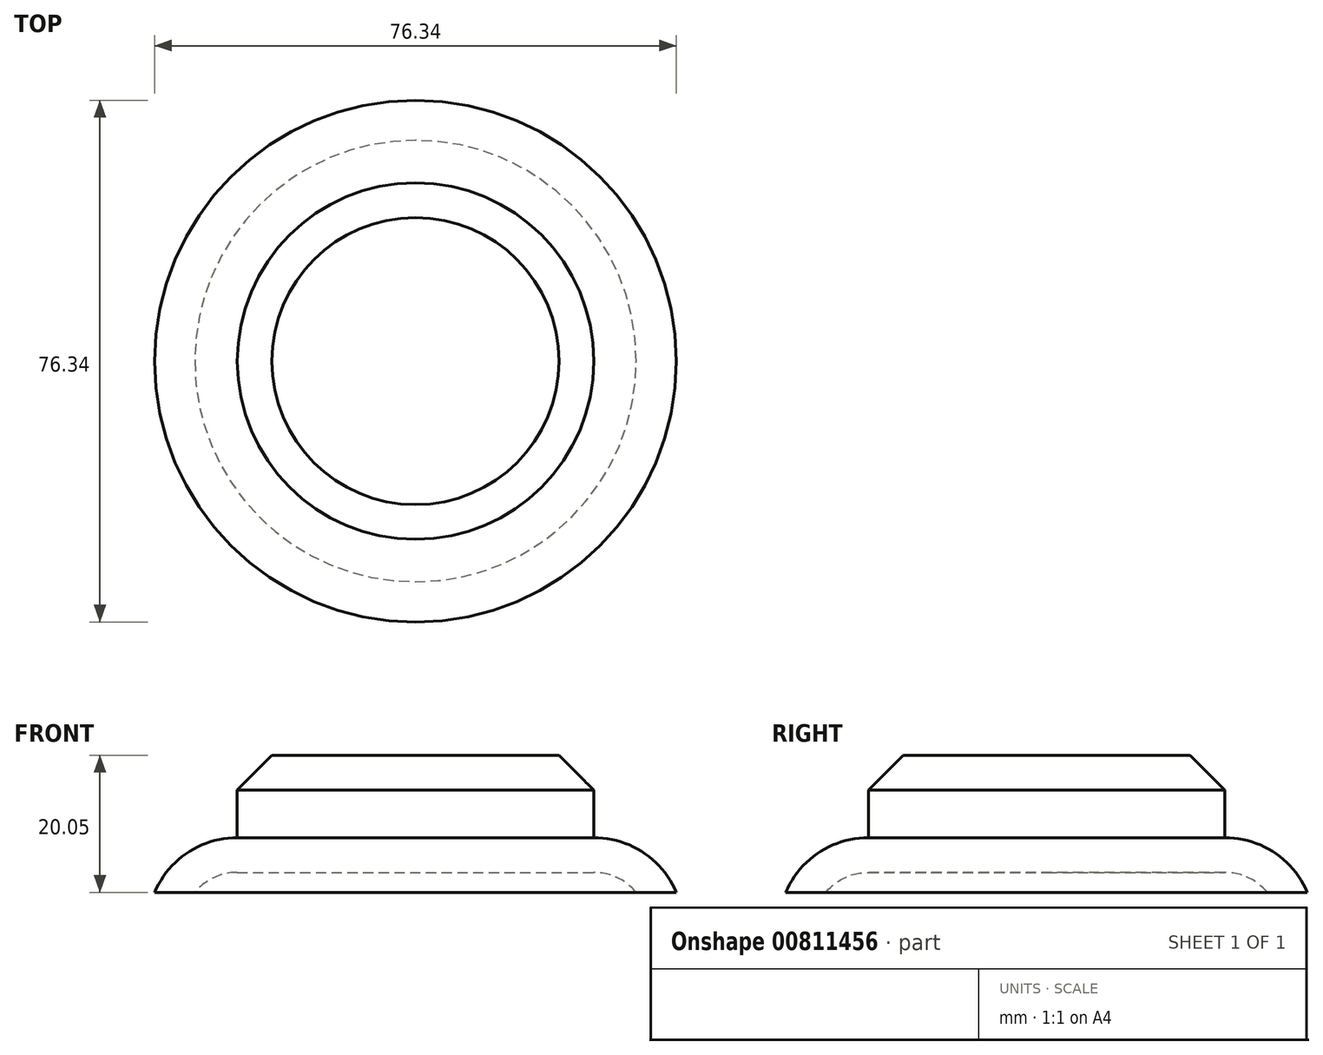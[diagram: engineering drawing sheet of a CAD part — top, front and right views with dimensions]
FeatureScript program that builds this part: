
annotation { "Feature Type Name" : "Feature", "Feature Type Description" : "" }
export const myFeature = defineFeature(function(context is Context, id is Id, definition is map)
    precondition{}
    {
        {
            var Q0;
            Q0=qCreatedBy(makeId("Top.planeOp"),FACE);
            var sketch = newSketch(context, id + "F0", { "sketchPlane" : qUnion([Q0])});
            skCircle(sketch, "E0", {"center": v(0, 0) * mm, "radius": 38.17 * mm});
            skSolve(sketch);
        }
        {
            var Q0;
            Q0=makeQuery(id+"F0.imprint","IMPRINT",FACE,{"disambiguationData":[TD([[makeQuery(id+"F0.imprint","IMPRINT",EDGE,{"derivedFrom":sQuery(id+"F0.wireOp",EDGE,"E0")}),1.0]])]});
            extrude(context, id + "F1", {"entities" : qUnion([Q0]), "depth" : 8 * mm, "offsetDistance" : 25.4 * mm});
        }
        {
            var Q0;
            Q0=makeQuery(id+"F1.opExtrude","CAP_FACE",FACE,{"disambiguationData":[OSD([sQuery(id+"F0.wireOp",EDGE,"E0")])],"isStart":false});
            fillet(context, id + "F2", {"entities" : qUnion([Q0]), "radius" : 13.13 * mm, "tangentPropagation" : true, "allowEdgeOverflow" : false});
        }
        {
            var Q0;
            Q0=makeQuery(id+"F1.opExtrude","CAP_FACE",FACE,{"disambiguationData":[OSD([sQuery(id+"F0.wireOp",EDGE,"E0")])],"isStart":true});
            shell(context, id + "F3", {"entities" : qUnion([Q0]), "thickness" : 5.08 * mm});
        }
        {
            var Q0;
            Q0=makeQuery(id+"F1.opExtrude","CAP_FACE",FACE,{"disambiguationData":[OSD([sQuery(id+"F0.wireOp",EDGE,"E0")])],"isStart":false});
            extrude(context, id + "F4", {"entities" : qUnion([Q0]), "operationType" : NewBodyOperationType.ADD, "depth" : 12.04 * mm, "offsetDistance" : 25.4 * mm});
        }
        {
            var Q0;
            Q0=makeQuery(id+"F4.opExtrude","CAP_FACE",FACE,{"disambiguationData":[OSD([sQuery(id+"F0.wireOp",EDGE,"E0")])],"isStart":false});
            chamfer(context, id + "F5", {"entities" : qUnion([Q0]), "width" : 5.08 * mm, "tangentPropagation" : true});
        }
    });
